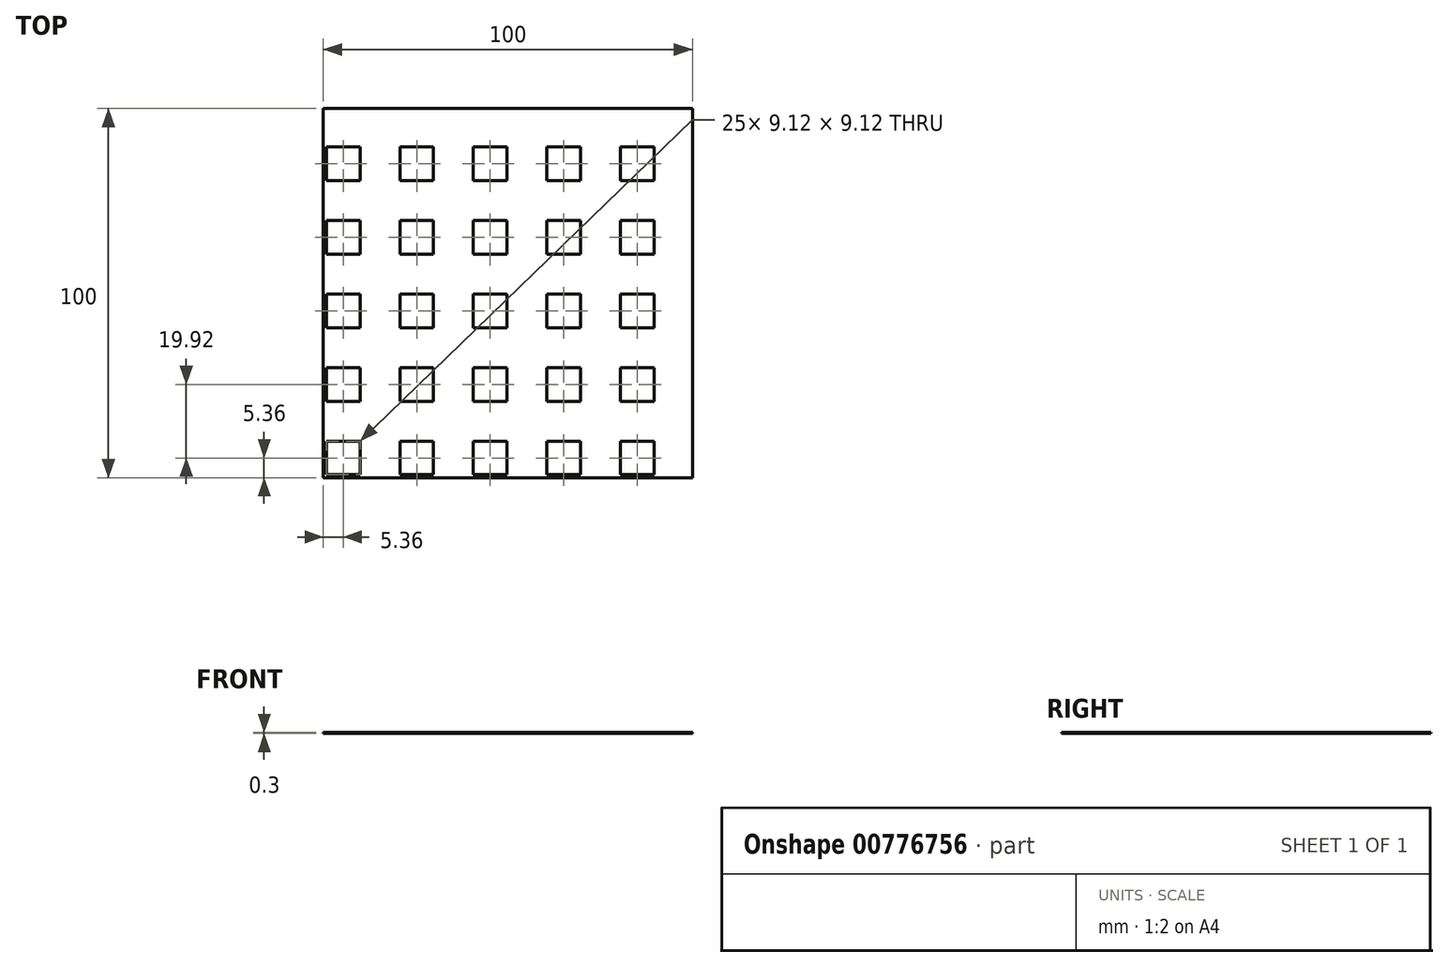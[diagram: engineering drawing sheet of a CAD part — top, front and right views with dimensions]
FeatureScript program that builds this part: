
annotation { "Feature Type Name" : "Feature", "Feature Type Description" : "" }
export const myFeature = defineFeature(function(context is Context, id is Id, definition is map)
    precondition{}
    {
        {
            var Q0;
            Q0=qCreatedBy(makeId("Top.planeOp"),FACE);
            var sketch = newSketch(context, id + "F0", { "sketchPlane" : qUnion([Q0])});
            skLineSegment(sketch, "E0.bottom", {"start": v(0, 0) * mm, "end": v(100, 0) * mm});
            skLineSegment(sketch, "E0.top", {"start": v(0, 100) * mm, "end": v(100, 100) * mm});
            skLineSegment(sketch, "E0.left", {"start": v(0, 0) * mm, "end": v(0, 100) * mm});
            skLineSegment(sketch, "E0.right", {"start": v(100, 0) * mm, "end": v(100, 100) * mm});
            skLineSegment(sketch, "E1.bottom", {"start": v(0.8, 0.8) * mm, "end": v(9.92, 0.8) * mm});
            skLineSegment(sketch, "E1.top", {"start": v(0.8, 9.92) * mm, "end": v(9.92, 9.92) * mm});
            skLineSegment(sketch, "E1.left", {"start": v(0.8, 0.8) * mm, "end": v(0.8, 9.92) * mm});
            skLineSegment(sketch, "E1.right", {"start": v(9.92, 0.8) * mm, "end": v(9.92, 9.92) * mm});
            skLineSegment(sketch, "E2.0.1.0", {"start": v(0.8, 29.84) * mm, "end": v(9.92, 29.84) * mm});
            skLineSegment(sketch, "E2.0.1.1", {"start": v(0.8, 20.72) * mm, "end": v(0.8, 29.84) * mm});
            skLineSegment(sketch, "E2.0.1.2", {"start": v(9.92, 20.72) * mm, "end": v(9.92, 29.84) * mm});
            skLineSegment(sketch, "E2.0.1.3", {"start": v(0.8, 20.72) * mm, "end": v(9.92, 20.72) * mm});
            skLineSegment(sketch, "E2.0.2.0", {"start": v(0.8, 49.76) * mm, "end": v(9.92, 49.76) * mm});
            skLineSegment(sketch, "E2.0.2.1", {"start": v(0.8, 40.64) * mm, "end": v(0.8, 49.76) * mm});
            skLineSegment(sketch, "E2.0.2.2", {"start": v(9.92, 40.64) * mm, "end": v(9.92, 49.76) * mm});
            skLineSegment(sketch, "E2.0.2.3", {"start": v(0.8, 40.64) * mm, "end": v(9.92, 40.64) * mm});
            skLineSegment(sketch, "E2.0.3.0", {"start": v(0.8, 69.68) * mm, "end": v(9.92, 69.68) * mm});
            skLineSegment(sketch, "E2.0.3.1", {"start": v(0.8, 60.56) * mm, "end": v(0.8, 69.68) * mm});
            skLineSegment(sketch, "E2.0.3.2", {"start": v(9.92, 60.56) * mm, "end": v(9.92, 69.68) * mm});
            skLineSegment(sketch, "E2.0.3.3", {"start": v(0.8, 60.56) * mm, "end": v(9.92, 60.56) * mm});
            skLineSegment(sketch, "E2.0.4.0", {"start": v(0.8, 89.6) * mm, "end": v(9.92, 89.6) * mm});
            skLineSegment(sketch, "E2.0.4.1", {"start": v(0.8, 80.48) * mm, "end": v(0.8, 89.6) * mm});
            skLineSegment(sketch, "E2.0.4.2", {"start": v(9.92, 80.48) * mm, "end": v(9.92, 89.6) * mm});
            skLineSegment(sketch, "E2.0.4.3", {"start": v(0.8, 80.48) * mm, "end": v(9.92, 80.48) * mm});
            skLineSegment(sketch, "E2.0.5.0", {"start": v(0.8, 109.52) * mm, "end": v(9.92, 109.52) * mm});
            skLineSegment(sketch, "E2.0.5.1", {"start": v(0.8, 100.4) * mm, "end": v(0.8, 109.52) * mm});
            skLineSegment(sketch, "E2.0.5.2", {"start": v(9.92, 100.4) * mm, "end": v(9.92, 109.52) * mm});
            skLineSegment(sketch, "E2.0.5.3", {"start": v(0.8, 100.4) * mm, "end": v(9.92, 100.4) * mm});
            skLineSegment(sketch, "E2.0.6.0", {"start": v(0.8, 129.44) * mm, "end": v(9.92, 129.44) * mm});
            skLineSegment(sketch, "E2.0.6.1", {"start": v(0.8, 120.32) * mm, "end": v(0.8, 129.44) * mm});
            skLineSegment(sketch, "E2.0.6.2", {"start": v(9.92, 120.32) * mm, "end": v(9.92, 129.44) * mm});
            skLineSegment(sketch, "E2.0.6.3", {"start": v(0.8, 120.32) * mm, "end": v(9.92, 120.32) * mm});
            skLineSegment(sketch, "E2.0.7.0", {"start": v(0.8, 149.36) * mm, "end": v(9.92, 149.36) * mm});
            skLineSegment(sketch, "E2.0.7.1", {"start": v(0.8, 140.24) * mm, "end": v(0.8, 149.36) * mm});
            skLineSegment(sketch, "E2.0.7.2", {"start": v(9.92, 140.24) * mm, "end": v(9.92, 149.36) * mm});
            skLineSegment(sketch, "E2.0.7.3", {"start": v(0.8, 140.24) * mm, "end": v(9.92, 140.24) * mm});
            skLineSegment(sketch, "E2.0.8.0", {"start": v(0.8, 169.28) * mm, "end": v(9.92, 169.28) * mm});
            skLineSegment(sketch, "E2.0.8.1", {"start": v(0.8, 160.16) * mm, "end": v(0.8, 169.28) * mm});
            skLineSegment(sketch, "E2.0.8.2", {"start": v(9.92, 160.16) * mm, "end": v(9.92, 169.28) * mm});
            skLineSegment(sketch, "E2.0.8.3", {"start": v(0.8, 160.16) * mm, "end": v(9.92, 160.16) * mm});
            skLineSegment(sketch, "E2.0.9.0", {"start": v(0.8, 189.2) * mm, "end": v(9.92, 189.2) * mm});
            skLineSegment(sketch, "E2.0.9.1", {"start": v(0.8, 180.08) * mm, "end": v(0.8, 189.2) * mm});
            skLineSegment(sketch, "E2.0.9.2", {"start": v(9.92, 180.08) * mm, "end": v(9.92, 189.2) * mm});
            skLineSegment(sketch, "E2.0.9.3", {"start": v(0.8, 180.08) * mm, "end": v(9.92, 180.08) * mm});
            skLineSegment(sketch, "E2.1.0.0", {"start": v(20.72, 9.92) * mm, "end": v(29.84, 9.92) * mm});
            skLineSegment(sketch, "E2.1.0.1", {"start": v(20.72, 0.8) * mm, "end": v(20.72, 9.92) * mm});
            skLineSegment(sketch, "E2.1.0.2", {"start": v(29.84, 0.8) * mm, "end": v(29.84, 9.92) * mm});
            skLineSegment(sketch, "E2.1.0.3", {"start": v(20.72, 0.8) * mm, "end": v(29.84, 0.8) * mm});
            skLineSegment(sketch, "E2.1.1.0", {"start": v(20.72, 29.84) * mm, "end": v(29.84, 29.84) * mm});
            skLineSegment(sketch, "E2.1.1.1", {"start": v(20.72, 20.72) * mm, "end": v(20.72, 29.84) * mm});
            skLineSegment(sketch, "E2.1.1.2", {"start": v(29.84, 20.72) * mm, "end": v(29.84, 29.84) * mm});
            skLineSegment(sketch, "E2.1.1.3", {"start": v(20.72, 20.72) * mm, "end": v(29.84, 20.72) * mm});
            skLineSegment(sketch, "E2.1.2.0", {"start": v(20.72, 49.76) * mm, "end": v(29.84, 49.76) * mm});
            skLineSegment(sketch, "E2.1.2.1", {"start": v(20.72, 40.64) * mm, "end": v(20.72, 49.76) * mm});
            skLineSegment(sketch, "E2.1.2.2", {"start": v(29.84, 40.64) * mm, "end": v(29.84, 49.76) * mm});
            skLineSegment(sketch, "E2.1.2.3", {"start": v(20.72, 40.64) * mm, "end": v(29.84, 40.64) * mm});
            skLineSegment(sketch, "E2.1.3.0", {"start": v(20.72, 69.68) * mm, "end": v(29.84, 69.68) * mm});
            skLineSegment(sketch, "E2.1.3.1", {"start": v(20.72, 60.56) * mm, "end": v(20.72, 69.68) * mm});
            skLineSegment(sketch, "E2.1.3.2", {"start": v(29.84, 60.56) * mm, "end": v(29.84, 69.68) * mm});
            skLineSegment(sketch, "E2.1.3.3", {"start": v(20.72, 60.56) * mm, "end": v(29.84, 60.56) * mm});
            skLineSegment(sketch, "E2.1.4.0", {"start": v(20.72, 89.6) * mm, "end": v(29.84, 89.6) * mm});
            skLineSegment(sketch, "E2.1.4.1", {"start": v(20.72, 80.48) * mm, "end": v(20.72, 89.6) * mm});
            skLineSegment(sketch, "E2.1.4.2", {"start": v(29.84, 80.48) * mm, "end": v(29.84, 89.6) * mm});
            skLineSegment(sketch, "E2.1.4.3", {"start": v(20.72, 80.48) * mm, "end": v(29.84, 80.48) * mm});
            skLineSegment(sketch, "E2.1.5.0", {"start": v(20.72, 109.52) * mm, "end": v(29.84, 109.52) * mm});
            skLineSegment(sketch, "E2.1.5.1", {"start": v(20.72, 100.4) * mm, "end": v(20.72, 109.52) * mm});
            skLineSegment(sketch, "E2.1.5.2", {"start": v(29.84, 100.4) * mm, "end": v(29.84, 109.52) * mm});
            skLineSegment(sketch, "E2.1.5.3", {"start": v(20.72, 100.4) * mm, "end": v(29.84, 100.4) * mm});
            skLineSegment(sketch, "E2.1.6.0", {"start": v(20.72, 129.44) * mm, "end": v(29.84, 129.44) * mm});
            skLineSegment(sketch, "E2.1.6.1", {"start": v(20.72, 120.32) * mm, "end": v(20.72, 129.44) * mm});
            skLineSegment(sketch, "E2.1.6.2", {"start": v(29.84, 120.32) * mm, "end": v(29.84, 129.44) * mm});
            skLineSegment(sketch, "E2.1.6.3", {"start": v(20.72, 120.32) * mm, "end": v(29.84, 120.32) * mm});
            skLineSegment(sketch, "E2.1.7.0", {"start": v(20.72, 149.36) * mm, "end": v(29.84, 149.36) * mm});
            skLineSegment(sketch, "E2.1.7.1", {"start": v(20.72, 140.24) * mm, "end": v(20.72, 149.36) * mm});
            skLineSegment(sketch, "E2.1.7.2", {"start": v(29.84, 140.24) * mm, "end": v(29.84, 149.36) * mm});
            skLineSegment(sketch, "E2.1.7.3", {"start": v(20.72, 140.24) * mm, "end": v(29.84, 140.24) * mm});
            skLineSegment(sketch, "E2.1.8.0", {"start": v(20.72, 169.28) * mm, "end": v(29.84, 169.28) * mm});
            skLineSegment(sketch, "E2.1.8.1", {"start": v(20.72, 160.16) * mm, "end": v(20.72, 169.28) * mm});
            skLineSegment(sketch, "E2.1.8.2", {"start": v(29.84, 160.16) * mm, "end": v(29.84, 169.28) * mm});
            skLineSegment(sketch, "E2.1.8.3", {"start": v(20.72, 160.16) * mm, "end": v(29.84, 160.16) * mm});
            skLineSegment(sketch, "E2.1.9.0", {"start": v(20.72, 189.2) * mm, "end": v(29.84, 189.2) * mm});
            skLineSegment(sketch, "E2.1.9.1", {"start": v(20.72, 180.08) * mm, "end": v(20.72, 189.2) * mm});
            skLineSegment(sketch, "E2.1.9.2", {"start": v(29.84, 180.08) * mm, "end": v(29.84, 189.2) * mm});
            skLineSegment(sketch, "E2.1.9.3", {"start": v(20.72, 180.08) * mm, "end": v(29.84, 180.08) * mm});
            skLineSegment(sketch, "E2.2.0.0", {"start": v(40.64, 9.92) * mm, "end": v(49.76, 9.92) * mm});
            skLineSegment(sketch, "E2.2.0.1", {"start": v(40.64, 0.8) * mm, "end": v(40.64, 9.92) * mm});
            skLineSegment(sketch, "E2.2.0.2", {"start": v(49.76, 0.8) * mm, "end": v(49.76, 9.92) * mm});
            skLineSegment(sketch, "E2.2.0.3", {"start": v(40.64, 0.8) * mm, "end": v(49.76, 0.8) * mm});
            skLineSegment(sketch, "E2.2.1.0", {"start": v(40.64, 29.84) * mm, "end": v(49.76, 29.84) * mm});
            skLineSegment(sketch, "E2.2.1.1", {"start": v(40.64, 20.72) * mm, "end": v(40.64, 29.84) * mm});
            skLineSegment(sketch, "E2.2.1.2", {"start": v(49.76, 20.72) * mm, "end": v(49.76, 29.84) * mm});
            skLineSegment(sketch, "E2.2.1.3", {"start": v(40.64, 20.72) * mm, "end": v(49.76, 20.72) * mm});
            skLineSegment(sketch, "E2.2.2.0", {"start": v(40.64, 49.76) * mm, "end": v(49.76, 49.76) * mm});
            skLineSegment(sketch, "E2.2.2.1", {"start": v(40.64, 40.64) * mm, "end": v(40.64, 49.76) * mm});
            skLineSegment(sketch, "E2.2.2.2", {"start": v(49.76, 40.64) * mm, "end": v(49.76, 49.76) * mm});
            skLineSegment(sketch, "E2.2.2.3", {"start": v(40.64, 40.64) * mm, "end": v(49.76, 40.64) * mm});
            skLineSegment(sketch, "E2.2.3.0", {"start": v(40.64, 69.68) * mm, "end": v(49.76, 69.68) * mm});
            skLineSegment(sketch, "E2.2.3.1", {"start": v(40.64, 60.56) * mm, "end": v(40.64, 69.68) * mm});
            skLineSegment(sketch, "E2.2.3.2", {"start": v(49.76, 60.56) * mm, "end": v(49.76, 69.68) * mm});
            skLineSegment(sketch, "E2.2.3.3", {"start": v(40.64, 60.56) * mm, "end": v(49.76, 60.56) * mm});
            skLineSegment(sketch, "E2.2.4.0", {"start": v(40.64, 89.6) * mm, "end": v(49.76, 89.6) * mm});
            skLineSegment(sketch, "E2.2.4.1", {"start": v(40.64, 80.48) * mm, "end": v(40.64, 89.6) * mm});
            skLineSegment(sketch, "E2.2.4.2", {"start": v(49.76, 80.48) * mm, "end": v(49.76, 89.6) * mm});
            skLineSegment(sketch, "E2.2.4.3", {"start": v(40.64, 80.48) * mm, "end": v(49.76, 80.48) * mm});
            skLineSegment(sketch, "E2.2.5.0", {"start": v(40.64, 109.52) * mm, "end": v(49.76, 109.52) * mm});
            skLineSegment(sketch, "E2.2.5.1", {"start": v(40.64, 100.4) * mm, "end": v(40.64, 109.52) * mm});
            skLineSegment(sketch, "E2.2.5.2", {"start": v(49.76, 100.4) * mm, "end": v(49.76, 109.52) * mm});
            skLineSegment(sketch, "E2.2.5.3", {"start": v(40.64, 100.4) * mm, "end": v(49.76, 100.4) * mm});
            skLineSegment(sketch, "E2.2.6.0", {"start": v(40.64, 129.44) * mm, "end": v(49.76, 129.44) * mm});
            skLineSegment(sketch, "E2.2.6.1", {"start": v(40.64, 120.32) * mm, "end": v(40.64, 129.44) * mm});
            skLineSegment(sketch, "E2.2.6.2", {"start": v(49.76, 120.32) * mm, "end": v(49.76, 129.44) * mm});
            skLineSegment(sketch, "E2.2.6.3", {"start": v(40.64, 120.32) * mm, "end": v(49.76, 120.32) * mm});
            skLineSegment(sketch, "E2.2.7.0", {"start": v(40.64, 149.36) * mm, "end": v(49.76, 149.36) * mm});
            skLineSegment(sketch, "E2.2.7.1", {"start": v(40.64, 140.24) * mm, "end": v(40.64, 149.36) * mm});
            skLineSegment(sketch, "E2.2.7.2", {"start": v(49.76, 140.24) * mm, "end": v(49.76, 149.36) * mm});
            skLineSegment(sketch, "E2.2.7.3", {"start": v(40.64, 140.24) * mm, "end": v(49.76, 140.24) * mm});
            skLineSegment(sketch, "E2.2.8.0", {"start": v(40.64, 169.28) * mm, "end": v(49.76, 169.28) * mm});
            skLineSegment(sketch, "E2.2.8.1", {"start": v(40.64, 160.16) * mm, "end": v(40.64, 169.28) * mm});
            skLineSegment(sketch, "E2.2.8.2", {"start": v(49.76, 160.16) * mm, "end": v(49.76, 169.28) * mm});
            skLineSegment(sketch, "E2.2.8.3", {"start": v(40.64, 160.16) * mm, "end": v(49.76, 160.16) * mm});
            skLineSegment(sketch, "E2.2.9.0", {"start": v(40.64, 189.2) * mm, "end": v(49.76, 189.2) * mm});
            skLineSegment(sketch, "E2.2.9.1", {"start": v(40.64, 180.08) * mm, "end": v(40.64, 189.2) * mm});
            skLineSegment(sketch, "E2.2.9.2", {"start": v(49.76, 180.08) * mm, "end": v(49.76, 189.2) * mm});
            skLineSegment(sketch, "E2.2.9.3", {"start": v(40.64, 180.08) * mm, "end": v(49.76, 180.08) * mm});
            skLineSegment(sketch, "E2.3.0.0", {"start": v(60.56, 9.92) * mm, "end": v(69.68, 9.92) * mm});
            skLineSegment(sketch, "E2.3.0.1", {"start": v(60.56, 0.8) * mm, "end": v(60.56, 9.92) * mm});
            skLineSegment(sketch, "E2.3.0.2", {"start": v(69.68, 0.8) * mm, "end": v(69.68, 9.92) * mm});
            skLineSegment(sketch, "E2.3.0.3", {"start": v(60.56, 0.8) * mm, "end": v(69.68, 0.8) * mm});
            skLineSegment(sketch, "E2.3.1.0", {"start": v(60.56, 29.84) * mm, "end": v(69.68, 29.84) * mm});
            skLineSegment(sketch, "E2.3.1.1", {"start": v(60.56, 20.72) * mm, "end": v(60.56, 29.84) * mm});
            skLineSegment(sketch, "E2.3.1.2", {"start": v(69.68, 20.72) * mm, "end": v(69.68, 29.84) * mm});
            skLineSegment(sketch, "E2.3.1.3", {"start": v(60.56, 20.72) * mm, "end": v(69.68, 20.72) * mm});
            skLineSegment(sketch, "E2.3.2.0", {"start": v(60.56, 49.76) * mm, "end": v(69.68, 49.76) * mm});
            skLineSegment(sketch, "E2.3.2.1", {"start": v(60.56, 40.64) * mm, "end": v(60.56, 49.76) * mm});
            skLineSegment(sketch, "E2.3.2.2", {"start": v(69.68, 40.64) * mm, "end": v(69.68, 49.76) * mm});
            skLineSegment(sketch, "E2.3.2.3", {"start": v(60.56, 40.64) * mm, "end": v(69.68, 40.64) * mm});
            skLineSegment(sketch, "E2.3.3.0", {"start": v(60.56, 69.68) * mm, "end": v(69.68, 69.68) * mm});
            skLineSegment(sketch, "E2.3.3.1", {"start": v(60.56, 60.56) * mm, "end": v(60.56, 69.68) * mm});
            skLineSegment(sketch, "E2.3.3.2", {"start": v(69.68, 60.56) * mm, "end": v(69.68, 69.68) * mm});
            skLineSegment(sketch, "E2.3.3.3", {"start": v(60.56, 60.56) * mm, "end": v(69.68, 60.56) * mm});
            skLineSegment(sketch, "E2.3.4.0", {"start": v(60.56, 89.6) * mm, "end": v(69.68, 89.6) * mm});
            skLineSegment(sketch, "E2.3.4.1", {"start": v(60.56, 80.48) * mm, "end": v(60.56, 89.6) * mm});
            skLineSegment(sketch, "E2.3.4.2", {"start": v(69.68, 80.48) * mm, "end": v(69.68, 89.6) * mm});
            skLineSegment(sketch, "E2.3.4.3", {"start": v(60.56, 80.48) * mm, "end": v(69.68, 80.48) * mm});
            skLineSegment(sketch, "E2.3.5.0", {"start": v(60.56, 109.52) * mm, "end": v(69.68, 109.52) * mm});
            skLineSegment(sketch, "E2.3.5.1", {"start": v(60.56, 100.4) * mm, "end": v(60.56, 109.52) * mm});
            skLineSegment(sketch, "E2.3.5.2", {"start": v(69.68, 100.4) * mm, "end": v(69.68, 109.52) * mm});
            skLineSegment(sketch, "E2.3.5.3", {"start": v(60.56, 100.4) * mm, "end": v(69.68, 100.4) * mm});
            skLineSegment(sketch, "E2.3.6.0", {"start": v(60.56, 129.44) * mm, "end": v(69.68, 129.44) * mm});
            skLineSegment(sketch, "E2.3.6.1", {"start": v(60.56, 120.32) * mm, "end": v(60.56, 129.44) * mm});
            skLineSegment(sketch, "E2.3.6.2", {"start": v(69.68, 120.32) * mm, "end": v(69.68, 129.44) * mm});
            skLineSegment(sketch, "E2.3.6.3", {"start": v(60.56, 120.32) * mm, "end": v(69.68, 120.32) * mm});
            skLineSegment(sketch, "E2.3.7.0", {"start": v(60.56, 149.36) * mm, "end": v(69.68, 149.36) * mm});
            skLineSegment(sketch, "E2.3.7.1", {"start": v(60.56, 140.24) * mm, "end": v(60.56, 149.36) * mm});
            skLineSegment(sketch, "E2.3.7.2", {"start": v(69.68, 140.24) * mm, "end": v(69.68, 149.36) * mm});
            skLineSegment(sketch, "E2.3.7.3", {"start": v(60.56, 140.24) * mm, "end": v(69.68, 140.24) * mm});
            skLineSegment(sketch, "E2.3.8.0", {"start": v(60.56, 169.28) * mm, "end": v(69.68, 169.28) * mm});
            skLineSegment(sketch, "E2.3.8.1", {"start": v(60.56, 160.16) * mm, "end": v(60.56, 169.28) * mm});
            skLineSegment(sketch, "E2.3.8.2", {"start": v(69.68, 160.16) * mm, "end": v(69.68, 169.28) * mm});
            skLineSegment(sketch, "E2.3.8.3", {"start": v(60.56, 160.16) * mm, "end": v(69.68, 160.16) * mm});
            skLineSegment(sketch, "E2.3.9.0", {"start": v(60.56, 189.2) * mm, "end": v(69.68, 189.2) * mm});
            skLineSegment(sketch, "E2.3.9.1", {"start": v(60.56, 180.08) * mm, "end": v(60.56, 189.2) * mm});
            skLineSegment(sketch, "E2.3.9.2", {"start": v(69.68, 180.08) * mm, "end": v(69.68, 189.2) * mm});
            skLineSegment(sketch, "E2.3.9.3", {"start": v(60.56, 180.08) * mm, "end": v(69.68, 180.08) * mm});
            skLineSegment(sketch, "E2.4.0.0", {"start": v(80.48, 9.92) * mm, "end": v(89.6, 9.92) * mm});
            skLineSegment(sketch, "E2.4.0.1", {"start": v(80.48, 0.8) * mm, "end": v(80.48, 9.92) * mm});
            skLineSegment(sketch, "E2.4.0.2", {"start": v(89.6, 0.8) * mm, "end": v(89.6, 9.92) * mm});
            skLineSegment(sketch, "E2.4.0.3", {"start": v(80.48, 0.8) * mm, "end": v(89.6, 0.8) * mm});
            skLineSegment(sketch, "E2.4.1.0", {"start": v(80.48, 29.84) * mm, "end": v(89.6, 29.84) * mm});
            skLineSegment(sketch, "E2.4.1.1", {"start": v(80.48, 20.72) * mm, "end": v(80.48, 29.84) * mm});
            skLineSegment(sketch, "E2.4.1.2", {"start": v(89.6, 20.72) * mm, "end": v(89.6, 29.84) * mm});
            skLineSegment(sketch, "E2.4.1.3", {"start": v(80.48, 20.72) * mm, "end": v(89.6, 20.72) * mm});
            skLineSegment(sketch, "E2.4.2.0", {"start": v(80.48, 49.76) * mm, "end": v(89.6, 49.76) * mm});
            skLineSegment(sketch, "E2.4.2.1", {"start": v(80.48, 40.64) * mm, "end": v(80.48, 49.76) * mm});
            skLineSegment(sketch, "E2.4.2.2", {"start": v(89.6, 40.64) * mm, "end": v(89.6, 49.76) * mm});
            skLineSegment(sketch, "E2.4.2.3", {"start": v(80.48, 40.64) * mm, "end": v(89.6, 40.64) * mm});
            skLineSegment(sketch, "E2.4.3.0", {"start": v(80.48, 69.68) * mm, "end": v(89.6, 69.68) * mm});
            skLineSegment(sketch, "E2.4.3.1", {"start": v(80.48, 60.56) * mm, "end": v(80.48, 69.68) * mm});
            skLineSegment(sketch, "E2.4.3.2", {"start": v(89.6, 60.56) * mm, "end": v(89.6, 69.68) * mm});
            skLineSegment(sketch, "E2.4.3.3", {"start": v(80.48, 60.56) * mm, "end": v(89.6, 60.56) * mm});
            skLineSegment(sketch, "E2.4.4.0", {"start": v(80.48, 89.6) * mm, "end": v(89.6, 89.6) * mm});
            skLineSegment(sketch, "E2.4.4.1", {"start": v(80.48, 80.48) * mm, "end": v(80.48, 89.6) * mm});
            skLineSegment(sketch, "E2.4.4.2", {"start": v(89.6, 80.48) * mm, "end": v(89.6, 89.6) * mm});
            skLineSegment(sketch, "E2.4.4.3", {"start": v(80.48, 80.48) * mm, "end": v(89.6, 80.48) * mm});
            skLineSegment(sketch, "E2.4.5.0", {"start": v(80.48, 109.52) * mm, "end": v(89.6, 109.52) * mm});
            skLineSegment(sketch, "E2.4.5.1", {"start": v(80.48, 100.4) * mm, "end": v(80.48, 109.52) * mm});
            skLineSegment(sketch, "E2.4.5.2", {"start": v(89.6, 100.4) * mm, "end": v(89.6, 109.52) * mm});
            skLineSegment(sketch, "E2.4.5.3", {"start": v(80.48, 100.4) * mm, "end": v(89.6, 100.4) * mm});
            skLineSegment(sketch, "E2.4.6.0", {"start": v(80.48, 129.44) * mm, "end": v(89.6, 129.44) * mm});
            skLineSegment(sketch, "E2.4.6.1", {"start": v(80.48, 120.32) * mm, "end": v(80.48, 129.44) * mm});
            skLineSegment(sketch, "E2.4.6.2", {"start": v(89.6, 120.32) * mm, "end": v(89.6, 129.44) * mm});
            skLineSegment(sketch, "E2.4.6.3", {"start": v(80.48, 120.32) * mm, "end": v(89.6, 120.32) * mm});
            skLineSegment(sketch, "E2.4.7.0", {"start": v(80.48, 149.36) * mm, "end": v(89.6, 149.36) * mm});
            skLineSegment(sketch, "E2.4.7.1", {"start": v(80.48, 140.24) * mm, "end": v(80.48, 149.36) * mm});
            skLineSegment(sketch, "E2.4.7.2", {"start": v(89.6, 140.24) * mm, "end": v(89.6, 149.36) * mm});
            skLineSegment(sketch, "E2.4.7.3", {"start": v(80.48, 140.24) * mm, "end": v(89.6, 140.24) * mm});
            skLineSegment(sketch, "E2.4.8.0", {"start": v(80.48, 169.28) * mm, "end": v(89.6, 169.28) * mm});
            skLineSegment(sketch, "E2.4.8.1", {"start": v(80.48, 160.16) * mm, "end": v(80.48, 169.28) * mm});
            skLineSegment(sketch, "E2.4.8.2", {"start": v(89.6, 160.16) * mm, "end": v(89.6, 169.28) * mm});
            skLineSegment(sketch, "E2.4.8.3", {"start": v(80.48, 160.16) * mm, "end": v(89.6, 160.16) * mm});
            skLineSegment(sketch, "E2.4.9.0", {"start": v(80.48, 189.2) * mm, "end": v(89.6, 189.2) * mm});
            skLineSegment(sketch, "E2.4.9.1", {"start": v(80.48, 180.08) * mm, "end": v(80.48, 189.2) * mm});
            skLineSegment(sketch, "E2.4.9.2", {"start": v(89.6, 180.08) * mm, "end": v(89.6, 189.2) * mm});
            skLineSegment(sketch, "E2.4.9.3", {"start": v(80.48, 180.08) * mm, "end": v(89.6, 180.08) * mm});
            skLineSegment(sketch, "E2.5.0.0", {"start": v(100.4, 9.92) * mm, "end": v(109.52, 9.92) * mm});
            skLineSegment(sketch, "E2.5.0.1", {"start": v(100.4, 0.8) * mm, "end": v(100.4, 9.92) * mm});
            skLineSegment(sketch, "E2.5.0.2", {"start": v(109.52, 0.8) * mm, "end": v(109.52, 9.92) * mm});
            skLineSegment(sketch, "E2.5.0.3", {"start": v(100.4, 0.8) * mm, "end": v(109.52, 0.8) * mm});
            skLineSegment(sketch, "E2.5.1.0", {"start": v(100.4, 29.84) * mm, "end": v(109.52, 29.84) * mm});
            skLineSegment(sketch, "E2.5.1.1", {"start": v(100.4, 20.72) * mm, "end": v(100.4, 29.84) * mm});
            skLineSegment(sketch, "E2.5.1.2", {"start": v(109.52, 20.72) * mm, "end": v(109.52, 29.84) * mm});
            skLineSegment(sketch, "E2.5.1.3", {"start": v(100.4, 20.72) * mm, "end": v(109.52, 20.72) * mm});
            skLineSegment(sketch, "E2.5.2.0", {"start": v(100.4, 49.76) * mm, "end": v(109.52, 49.76) * mm});
            skLineSegment(sketch, "E2.5.2.1", {"start": v(100.4, 40.64) * mm, "end": v(100.4, 49.76) * mm});
            skLineSegment(sketch, "E2.5.2.2", {"start": v(109.52, 40.64) * mm, "end": v(109.52, 49.76) * mm});
            skLineSegment(sketch, "E2.5.2.3", {"start": v(100.4, 40.64) * mm, "end": v(109.52, 40.64) * mm});
            skLineSegment(sketch, "E2.5.3.0", {"start": v(100.4, 69.68) * mm, "end": v(109.52, 69.68) * mm});
            skLineSegment(sketch, "E2.5.3.1", {"start": v(100.4, 60.56) * mm, "end": v(100.4, 69.68) * mm});
            skLineSegment(sketch, "E2.5.3.2", {"start": v(109.52, 60.56) * mm, "end": v(109.52, 69.68) * mm});
            skLineSegment(sketch, "E2.5.3.3", {"start": v(100.4, 60.56) * mm, "end": v(109.52, 60.56) * mm});
            skLineSegment(sketch, "E2.5.4.0", {"start": v(100.4, 89.6) * mm, "end": v(109.52, 89.6) * mm});
            skLineSegment(sketch, "E2.5.4.1", {"start": v(100.4, 80.48) * mm, "end": v(100.4, 89.6) * mm});
            skLineSegment(sketch, "E2.5.4.2", {"start": v(109.52, 80.48) * mm, "end": v(109.52, 89.6) * mm});
            skLineSegment(sketch, "E2.5.4.3", {"start": v(100.4, 80.48) * mm, "end": v(109.52, 80.48) * mm});
            skLineSegment(sketch, "E2.5.5.0", {"start": v(100.4, 109.52) * mm, "end": v(109.52, 109.52) * mm});
            skLineSegment(sketch, "E2.5.5.1", {"start": v(100.4, 100.4) * mm, "end": v(100.4, 109.52) * mm});
            skLineSegment(sketch, "E2.5.5.2", {"start": v(109.52, 100.4) * mm, "end": v(109.52, 109.52) * mm});
            skLineSegment(sketch, "E2.5.5.3", {"start": v(100.4, 100.4) * mm, "end": v(109.52, 100.4) * mm});
            skLineSegment(sketch, "E2.5.6.0", {"start": v(100.4, 129.44) * mm, "end": v(109.52, 129.44) * mm});
            skLineSegment(sketch, "E2.5.6.1", {"start": v(100.4, 120.32) * mm, "end": v(100.4, 129.44) * mm});
            skLineSegment(sketch, "E2.5.6.2", {"start": v(109.52, 120.32) * mm, "end": v(109.52, 129.44) * mm});
            skLineSegment(sketch, "E2.5.6.3", {"start": v(100.4, 120.32) * mm, "end": v(109.52, 120.32) * mm});
            skLineSegment(sketch, "E2.5.7.0", {"start": v(100.4, 149.36) * mm, "end": v(109.52, 149.36) * mm});
            skLineSegment(sketch, "E2.5.7.1", {"start": v(100.4, 140.24) * mm, "end": v(100.4, 149.36) * mm});
            skLineSegment(sketch, "E2.5.7.2", {"start": v(109.52, 140.24) * mm, "end": v(109.52, 149.36) * mm});
            skLineSegment(sketch, "E2.5.7.3", {"start": v(100.4, 140.24) * mm, "end": v(109.52, 140.24) * mm});
            skLineSegment(sketch, "E2.5.8.0", {"start": v(100.4, 169.28) * mm, "end": v(109.52, 169.28) * mm});
            skLineSegment(sketch, "E2.5.8.1", {"start": v(100.4, 160.16) * mm, "end": v(100.4, 169.28) * mm});
            skLineSegment(sketch, "E2.5.8.2", {"start": v(109.52, 160.16) * mm, "end": v(109.52, 169.28) * mm});
            skLineSegment(sketch, "E2.5.8.3", {"start": v(100.4, 160.16) * mm, "end": v(109.52, 160.16) * mm});
            skLineSegment(sketch, "E2.5.9.0", {"start": v(100.4, 189.2) * mm, "end": v(109.52, 189.2) * mm});
            skLineSegment(sketch, "E2.5.9.1", {"start": v(100.4, 180.08) * mm, "end": v(100.4, 189.2) * mm});
            skLineSegment(sketch, "E2.5.9.2", {"start": v(109.52, 180.08) * mm, "end": v(109.52, 189.2) * mm});
            skLineSegment(sketch, "E2.5.9.3", {"start": v(100.4, 180.08) * mm, "end": v(109.52, 180.08) * mm});
            skLineSegment(sketch, "E2.6.0.0", {"start": v(120.32, 9.92) * mm, "end": v(129.44, 9.92) * mm});
            skLineSegment(sketch, "E2.6.0.1", {"start": v(120.32, 0.8) * mm, "end": v(120.32, 9.92) * mm});
            skLineSegment(sketch, "E2.6.0.2", {"start": v(129.44, 0.8) * mm, "end": v(129.44, 9.92) * mm});
            skLineSegment(sketch, "E2.6.0.3", {"start": v(120.32, 0.8) * mm, "end": v(129.44, 0.8) * mm});
            skLineSegment(sketch, "E2.6.1.0", {"start": v(120.32, 29.84) * mm, "end": v(129.44, 29.84) * mm});
            skLineSegment(sketch, "E2.6.1.1", {"start": v(120.32, 20.72) * mm, "end": v(120.32, 29.84) * mm});
            skLineSegment(sketch, "E2.6.1.2", {"start": v(129.44, 20.72) * mm, "end": v(129.44, 29.84) * mm});
            skLineSegment(sketch, "E2.6.1.3", {"start": v(120.32, 20.72) * mm, "end": v(129.44, 20.72) * mm});
            skLineSegment(sketch, "E2.6.2.0", {"start": v(120.32, 49.76) * mm, "end": v(129.44, 49.76) * mm});
            skLineSegment(sketch, "E2.6.2.1", {"start": v(120.32, 40.64) * mm, "end": v(120.32, 49.76) * mm});
            skLineSegment(sketch, "E2.6.2.2", {"start": v(129.44, 40.64) * mm, "end": v(129.44, 49.76) * mm});
            skLineSegment(sketch, "E2.6.2.3", {"start": v(120.32, 40.64) * mm, "end": v(129.44, 40.64) * mm});
            skLineSegment(sketch, "E2.6.3.0", {"start": v(120.32, 69.68) * mm, "end": v(129.44, 69.68) * mm});
            skLineSegment(sketch, "E2.6.3.1", {"start": v(120.32, 60.56) * mm, "end": v(120.32, 69.68) * mm});
            skLineSegment(sketch, "E2.6.3.2", {"start": v(129.44, 60.56) * mm, "end": v(129.44, 69.68) * mm});
            skLineSegment(sketch, "E2.6.3.3", {"start": v(120.32, 60.56) * mm, "end": v(129.44, 60.56) * mm});
            skLineSegment(sketch, "E2.6.4.0", {"start": v(120.32, 89.6) * mm, "end": v(129.44, 89.6) * mm});
            skLineSegment(sketch, "E2.6.4.1", {"start": v(120.32, 80.48) * mm, "end": v(120.32, 89.6) * mm});
            skLineSegment(sketch, "E2.6.4.2", {"start": v(129.44, 80.48) * mm, "end": v(129.44, 89.6) * mm});
            skLineSegment(sketch, "E2.6.4.3", {"start": v(120.32, 80.48) * mm, "end": v(129.44, 80.48) * mm});
            skLineSegment(sketch, "E2.6.5.0", {"start": v(120.32, 109.52) * mm, "end": v(129.44, 109.52) * mm});
            skLineSegment(sketch, "E2.6.5.1", {"start": v(120.32, 100.4) * mm, "end": v(120.32, 109.52) * mm});
            skLineSegment(sketch, "E2.6.5.2", {"start": v(129.44, 100.4) * mm, "end": v(129.44, 109.52) * mm});
            skLineSegment(sketch, "E2.6.5.3", {"start": v(120.32, 100.4) * mm, "end": v(129.44, 100.4) * mm});
            skLineSegment(sketch, "E2.6.6.0", {"start": v(120.32, 129.44) * mm, "end": v(129.44, 129.44) * mm});
            skLineSegment(sketch, "E2.6.6.1", {"start": v(120.32, 120.32) * mm, "end": v(120.32, 129.44) * mm});
            skLineSegment(sketch, "E2.6.6.2", {"start": v(129.44, 120.32) * mm, "end": v(129.44, 129.44) * mm});
            skLineSegment(sketch, "E2.6.6.3", {"start": v(120.32, 120.32) * mm, "end": v(129.44, 120.32) * mm});
            skLineSegment(sketch, "E2.6.7.0", {"start": v(120.32, 149.36) * mm, "end": v(129.44, 149.36) * mm});
            skLineSegment(sketch, "E2.6.7.1", {"start": v(120.32, 140.24) * mm, "end": v(120.32, 149.36) * mm});
            skLineSegment(sketch, "E2.6.7.2", {"start": v(129.44, 140.24) * mm, "end": v(129.44, 149.36) * mm});
            skLineSegment(sketch, "E2.6.7.3", {"start": v(120.32, 140.24) * mm, "end": v(129.44, 140.24) * mm});
            skLineSegment(sketch, "E2.6.8.0", {"start": v(120.32, 169.28) * mm, "end": v(129.44, 169.28) * mm});
            skLineSegment(sketch, "E2.6.8.1", {"start": v(120.32, 160.16) * mm, "end": v(120.32, 169.28) * mm});
            skLineSegment(sketch, "E2.6.8.2", {"start": v(129.44, 160.16) * mm, "end": v(129.44, 169.28) * mm});
            skLineSegment(sketch, "E2.6.8.3", {"start": v(120.32, 160.16) * mm, "end": v(129.44, 160.16) * mm});
            skLineSegment(sketch, "E2.6.9.0", {"start": v(120.32, 189.2) * mm, "end": v(129.44, 189.2) * mm});
            skLineSegment(sketch, "E2.6.9.1", {"start": v(120.32, 180.08) * mm, "end": v(120.32, 189.2) * mm});
            skLineSegment(sketch, "E2.6.9.2", {"start": v(129.44, 180.08) * mm, "end": v(129.44, 189.2) * mm});
            skLineSegment(sketch, "E2.6.9.3", {"start": v(120.32, 180.08) * mm, "end": v(129.44, 180.08) * mm});
            skLineSegment(sketch, "E2.7.0.0", {"start": v(140.24, 9.92) * mm, "end": v(149.36, 9.92) * mm});
            skLineSegment(sketch, "E2.7.0.1", {"start": v(140.24, 0.8) * mm, "end": v(140.24, 9.92) * mm});
            skLineSegment(sketch, "E2.7.0.2", {"start": v(149.36, 0.8) * mm, "end": v(149.36, 9.92) * mm});
            skLineSegment(sketch, "E2.7.0.3", {"start": v(140.24, 0.8) * mm, "end": v(149.36, 0.8) * mm});
            skLineSegment(sketch, "E2.7.1.0", {"start": v(140.24, 29.84) * mm, "end": v(149.36, 29.84) * mm});
            skLineSegment(sketch, "E2.7.1.1", {"start": v(140.24, 20.72) * mm, "end": v(140.24, 29.84) * mm});
            skLineSegment(sketch, "E2.7.1.2", {"start": v(149.36, 20.72) * mm, "end": v(149.36, 29.84) * mm});
            skLineSegment(sketch, "E2.7.1.3", {"start": v(140.24, 20.72) * mm, "end": v(149.36, 20.72) * mm});
            skLineSegment(sketch, "E2.7.2.0", {"start": v(140.24, 49.76) * mm, "end": v(149.36, 49.76) * mm});
            skLineSegment(sketch, "E2.7.2.1", {"start": v(140.24, 40.64) * mm, "end": v(140.24, 49.76) * mm});
            skLineSegment(sketch, "E2.7.2.2", {"start": v(149.36, 40.64) * mm, "end": v(149.36, 49.76) * mm});
            skLineSegment(sketch, "E2.7.2.3", {"start": v(140.24, 40.64) * mm, "end": v(149.36, 40.64) * mm});
            skLineSegment(sketch, "E2.7.3.0", {"start": v(140.24, 69.68) * mm, "end": v(149.36, 69.68) * mm});
            skLineSegment(sketch, "E2.7.3.1", {"start": v(140.24, 60.56) * mm, "end": v(140.24, 69.68) * mm});
            skLineSegment(sketch, "E2.7.3.2", {"start": v(149.36, 60.56) * mm, "end": v(149.36, 69.68) * mm});
            skLineSegment(sketch, "E2.7.3.3", {"start": v(140.24, 60.56) * mm, "end": v(149.36, 60.56) * mm});
            skLineSegment(sketch, "E2.7.4.0", {"start": v(140.24, 89.6) * mm, "end": v(149.36, 89.6) * mm});
            skLineSegment(sketch, "E2.7.4.1", {"start": v(140.24, 80.48) * mm, "end": v(140.24, 89.6) * mm});
            skLineSegment(sketch, "E2.7.4.2", {"start": v(149.36, 80.48) * mm, "end": v(149.36, 89.6) * mm});
            skLineSegment(sketch, "E2.7.4.3", {"start": v(140.24, 80.48) * mm, "end": v(149.36, 80.48) * mm});
            skLineSegment(sketch, "E2.7.5.0", {"start": v(140.24, 109.52) * mm, "end": v(149.36, 109.52) * mm});
            skLineSegment(sketch, "E2.7.5.1", {"start": v(140.24, 100.4) * mm, "end": v(140.24, 109.52) * mm});
            skLineSegment(sketch, "E2.7.5.2", {"start": v(149.36, 100.4) * mm, "end": v(149.36, 109.52) * mm});
            skLineSegment(sketch, "E2.7.5.3", {"start": v(140.24, 100.4) * mm, "end": v(149.36, 100.4) * mm});
            skLineSegment(sketch, "E2.7.6.0", {"start": v(140.24, 129.44) * mm, "end": v(149.36, 129.44) * mm});
            skLineSegment(sketch, "E2.7.6.1", {"start": v(140.24, 120.32) * mm, "end": v(140.24, 129.44) * mm});
            skLineSegment(sketch, "E2.7.6.2", {"start": v(149.36, 120.32) * mm, "end": v(149.36, 129.44) * mm});
            skLineSegment(sketch, "E2.7.6.3", {"start": v(140.24, 120.32) * mm, "end": v(149.36, 120.32) * mm});
            skLineSegment(sketch, "E2.7.7.0", {"start": v(140.24, 149.36) * mm, "end": v(149.36, 149.36) * mm});
            skLineSegment(sketch, "E2.7.7.1", {"start": v(140.24, 140.24) * mm, "end": v(140.24, 149.36) * mm});
            skLineSegment(sketch, "E2.7.7.2", {"start": v(149.36, 140.24) * mm, "end": v(149.36, 149.36) * mm});
            skLineSegment(sketch, "E2.7.7.3", {"start": v(140.24, 140.24) * mm, "end": v(149.36, 140.24) * mm});
            skLineSegment(sketch, "E2.7.8.0", {"start": v(140.24, 169.28) * mm, "end": v(149.36, 169.28) * mm});
            skLineSegment(sketch, "E2.7.8.1", {"start": v(140.24, 160.16) * mm, "end": v(140.24, 169.28) * mm});
            skLineSegment(sketch, "E2.7.8.2", {"start": v(149.36, 160.16) * mm, "end": v(149.36, 169.28) * mm});
            skLineSegment(sketch, "E2.7.8.3", {"start": v(140.24, 160.16) * mm, "end": v(149.36, 160.16) * mm});
            skLineSegment(sketch, "E2.7.9.0", {"start": v(140.24, 189.2) * mm, "end": v(149.36, 189.2) * mm});
            skLineSegment(sketch, "E2.7.9.1", {"start": v(140.24, 180.08) * mm, "end": v(140.24, 189.2) * mm});
            skLineSegment(sketch, "E2.7.9.2", {"start": v(149.36, 180.08) * mm, "end": v(149.36, 189.2) * mm});
            skLineSegment(sketch, "E2.7.9.3", {"start": v(140.24, 180.08) * mm, "end": v(149.36, 180.08) * mm});
            skLineSegment(sketch, "E2.8.0.0", {"start": v(160.16, 9.92) * mm, "end": v(169.28, 9.92) * mm});
            skLineSegment(sketch, "E2.8.0.1", {"start": v(160.16, 0.8) * mm, "end": v(160.16, 9.92) * mm});
            skLineSegment(sketch, "E2.8.0.2", {"start": v(169.28, 0.8) * mm, "end": v(169.28, 9.92) * mm});
            skLineSegment(sketch, "E2.8.0.3", {"start": v(160.16, 0.8) * mm, "end": v(169.28, 0.8) * mm});
            skLineSegment(sketch, "E2.8.1.0", {"start": v(160.16, 29.84) * mm, "end": v(169.28, 29.84) * mm});
            skLineSegment(sketch, "E2.8.1.1", {"start": v(160.16, 20.72) * mm, "end": v(160.16, 29.84) * mm});
            skLineSegment(sketch, "E2.8.1.2", {"start": v(169.28, 20.72) * mm, "end": v(169.28, 29.84) * mm});
            skLineSegment(sketch, "E2.8.1.3", {"start": v(160.16, 20.72) * mm, "end": v(169.28, 20.72) * mm});
            skLineSegment(sketch, "E2.8.2.0", {"start": v(160.16, 49.76) * mm, "end": v(169.28, 49.76) * mm});
            skLineSegment(sketch, "E2.8.2.1", {"start": v(160.16, 40.64) * mm, "end": v(160.16, 49.76) * mm});
            skLineSegment(sketch, "E2.8.2.2", {"start": v(169.28, 40.64) * mm, "end": v(169.28, 49.76) * mm});
            skLineSegment(sketch, "E2.8.2.3", {"start": v(160.16, 40.64) * mm, "end": v(169.28, 40.64) * mm});
            skLineSegment(sketch, "E2.8.3.0", {"start": v(160.16, 69.68) * mm, "end": v(169.28, 69.68) * mm});
            skLineSegment(sketch, "E2.8.3.1", {"start": v(160.16, 60.56) * mm, "end": v(160.16, 69.68) * mm});
            skLineSegment(sketch, "E2.8.3.2", {"start": v(169.28, 60.56) * mm, "end": v(169.28, 69.68) * mm});
            skLineSegment(sketch, "E2.8.3.3", {"start": v(160.16, 60.56) * mm, "end": v(169.28, 60.56) * mm});
            skLineSegment(sketch, "E2.8.4.0", {"start": v(160.16, 89.6) * mm, "end": v(169.28, 89.6) * mm});
            skLineSegment(sketch, "E2.8.4.1", {"start": v(160.16, 80.48) * mm, "end": v(160.16, 89.6) * mm});
            skLineSegment(sketch, "E2.8.4.2", {"start": v(169.28, 80.48) * mm, "end": v(169.28, 89.6) * mm});
            skLineSegment(sketch, "E2.8.4.3", {"start": v(160.16, 80.48) * mm, "end": v(169.28, 80.48) * mm});
            skLineSegment(sketch, "E2.8.5.0", {"start": v(160.16, 109.52) * mm, "end": v(169.28, 109.52) * mm});
            skLineSegment(sketch, "E2.8.5.1", {"start": v(160.16, 100.4) * mm, "end": v(160.16, 109.52) * mm});
            skLineSegment(sketch, "E2.8.5.2", {"start": v(169.28, 100.4) * mm, "end": v(169.28, 109.52) * mm});
            skLineSegment(sketch, "E2.8.5.3", {"start": v(160.16, 100.4) * mm, "end": v(169.28, 100.4) * mm});
            skLineSegment(sketch, "E2.8.6.0", {"start": v(160.16, 129.44) * mm, "end": v(169.28, 129.44) * mm});
            skLineSegment(sketch, "E2.8.6.1", {"start": v(160.16, 120.32) * mm, "end": v(160.16, 129.44) * mm});
            skLineSegment(sketch, "E2.8.6.2", {"start": v(169.28, 120.32) * mm, "end": v(169.28, 129.44) * mm});
            skLineSegment(sketch, "E2.8.6.3", {"start": v(160.16, 120.32) * mm, "end": v(169.28, 120.32) * mm});
            skLineSegment(sketch, "E2.8.7.0", {"start": v(160.16, 149.36) * mm, "end": v(169.28, 149.36) * mm});
            skLineSegment(sketch, "E2.8.7.1", {"start": v(160.16, 140.24) * mm, "end": v(160.16, 149.36) * mm});
            skLineSegment(sketch, "E2.8.7.2", {"start": v(169.28, 140.24) * mm, "end": v(169.28, 149.36) * mm});
            skLineSegment(sketch, "E2.8.7.3", {"start": v(160.16, 140.24) * mm, "end": v(169.28, 140.24) * mm});
            skLineSegment(sketch, "E2.8.8.0", {"start": v(160.16, 169.28) * mm, "end": v(169.28, 169.28) * mm});
            skLineSegment(sketch, "E2.8.8.1", {"start": v(160.16, 160.16) * mm, "end": v(160.16, 169.28) * mm});
            skLineSegment(sketch, "E2.8.8.2", {"start": v(169.28, 160.16) * mm, "end": v(169.28, 169.28) * mm});
            skLineSegment(sketch, "E2.8.8.3", {"start": v(160.16, 160.16) * mm, "end": v(169.28, 160.16) * mm});
            skLineSegment(sketch, "E2.8.9.0", {"start": v(160.16, 189.2) * mm, "end": v(169.28, 189.2) * mm});
            skLineSegment(sketch, "E2.8.9.1", {"start": v(160.16, 180.08) * mm, "end": v(160.16, 189.2) * mm});
            skLineSegment(sketch, "E2.8.9.2", {"start": v(169.28, 180.08) * mm, "end": v(169.28, 189.2) * mm});
            skLineSegment(sketch, "E2.8.9.3", {"start": v(160.16, 180.08) * mm, "end": v(169.28, 180.08) * mm});
            skLineSegment(sketch, "E2.9.0.0", {"start": v(180.08, 9.92) * mm, "end": v(189.2, 9.92) * mm});
            skLineSegment(sketch, "E2.9.0.1", {"start": v(180.08, 0.8) * mm, "end": v(180.08, 9.92) * mm});
            skLineSegment(sketch, "E2.9.0.2", {"start": v(189.2, 0.8) * mm, "end": v(189.2, 9.92) * mm});
            skLineSegment(sketch, "E2.9.0.3", {"start": v(180.08, 0.8) * mm, "end": v(189.2, 0.8) * mm});
            skLineSegment(sketch, "E2.9.1.0", {"start": v(180.08, 29.84) * mm, "end": v(189.2, 29.84) * mm});
            skLineSegment(sketch, "E2.9.1.1", {"start": v(180.08, 20.72) * mm, "end": v(180.08, 29.84) * mm});
            skLineSegment(sketch, "E2.9.1.2", {"start": v(189.2, 20.72) * mm, "end": v(189.2, 29.84) * mm});
            skLineSegment(sketch, "E2.9.1.3", {"start": v(180.08, 20.72) * mm, "end": v(189.2, 20.72) * mm});
            skLineSegment(sketch, "E2.9.2.0", {"start": v(180.08, 49.76) * mm, "end": v(189.2, 49.76) * mm});
            skLineSegment(sketch, "E2.9.2.1", {"start": v(180.08, 40.64) * mm, "end": v(180.08, 49.76) * mm});
            skLineSegment(sketch, "E2.9.2.2", {"start": v(189.2, 40.64) * mm, "end": v(189.2, 49.76) * mm});
            skLineSegment(sketch, "E2.9.2.3", {"start": v(180.08, 40.64) * mm, "end": v(189.2, 40.64) * mm});
            skLineSegment(sketch, "E2.9.3.0", {"start": v(180.08, 69.68) * mm, "end": v(189.2, 69.68) * mm});
            skLineSegment(sketch, "E2.9.3.1", {"start": v(180.08, 60.56) * mm, "end": v(180.08, 69.68) * mm});
            skLineSegment(sketch, "E2.9.3.2", {"start": v(189.2, 60.56) * mm, "end": v(189.2, 69.68) * mm});
            skLineSegment(sketch, "E2.9.3.3", {"start": v(180.08, 60.56) * mm, "end": v(189.2, 60.56) * mm});
            skLineSegment(sketch, "E2.9.4.0", {"start": v(180.08, 89.6) * mm, "end": v(189.2, 89.6) * mm});
            skLineSegment(sketch, "E2.9.4.1", {"start": v(180.08, 80.48) * mm, "end": v(180.08, 89.6) * mm});
            skLineSegment(sketch, "E2.9.4.2", {"start": v(189.2, 80.48) * mm, "end": v(189.2, 89.6) * mm});
            skLineSegment(sketch, "E2.9.4.3", {"start": v(180.08, 80.48) * mm, "end": v(189.2, 80.48) * mm});
            skLineSegment(sketch, "E2.9.5.0", {"start": v(180.08, 109.52) * mm, "end": v(189.2, 109.52) * mm});
            skLineSegment(sketch, "E2.9.5.1", {"start": v(180.08, 100.4) * mm, "end": v(180.08, 109.52) * mm});
            skLineSegment(sketch, "E2.9.5.2", {"start": v(189.2, 100.4) * mm, "end": v(189.2, 109.52) * mm});
            skLineSegment(sketch, "E2.9.5.3", {"start": v(180.08, 100.4) * mm, "end": v(189.2, 100.4) * mm});
            skLineSegment(sketch, "E2.9.6.0", {"start": v(180.08, 129.44) * mm, "end": v(189.2, 129.44) * mm});
            skLineSegment(sketch, "E2.9.6.1", {"start": v(180.08, 120.32) * mm, "end": v(180.08, 129.44) * mm});
            skLineSegment(sketch, "E2.9.6.2", {"start": v(189.2, 120.32) * mm, "end": v(189.2, 129.44) * mm});
            skLineSegment(sketch, "E2.9.6.3", {"start": v(180.08, 120.32) * mm, "end": v(189.2, 120.32) * mm});
            skLineSegment(sketch, "E2.9.7.0", {"start": v(180.08, 149.36) * mm, "end": v(189.2, 149.36) * mm});
            skLineSegment(sketch, "E2.9.7.1", {"start": v(180.08, 140.24) * mm, "end": v(180.08, 149.36) * mm});
            skLineSegment(sketch, "E2.9.7.2", {"start": v(189.2, 140.24) * mm, "end": v(189.2, 149.36) * mm});
            skLineSegment(sketch, "E2.9.7.3", {"start": v(180.08, 140.24) * mm, "end": v(189.2, 140.24) * mm});
            skLineSegment(sketch, "E2.9.8.0", {"start": v(180.08, 169.28) * mm, "end": v(189.2, 169.28) * mm});
            skLineSegment(sketch, "E2.9.8.1", {"start": v(180.08, 160.16) * mm, "end": v(180.08, 169.28) * mm});
            skLineSegment(sketch, "E2.9.8.2", {"start": v(189.2, 160.16) * mm, "end": v(189.2, 169.28) * mm});
            skLineSegment(sketch, "E2.9.8.3", {"start": v(180.08, 160.16) * mm, "end": v(189.2, 160.16) * mm});
            skLineSegment(sketch, "E2.9.9.0", {"start": v(180.08, 189.2) * mm, "end": v(189.2, 189.2) * mm});
            skLineSegment(sketch, "E2.9.9.1", {"start": v(180.08, 180.08) * mm, "end": v(180.08, 189.2) * mm});
            skLineSegment(sketch, "E2.9.9.2", {"start": v(189.2, 180.08) * mm, "end": v(189.2, 189.2) * mm});
            skLineSegment(sketch, "E2.9.9.3", {"start": v(180.08, 180.08) * mm, "end": v(189.2, 180.08) * mm});
            skLineSegment(sketch, "E2.direction1", {"start": v(0.8, 20.8) * mm, "end": v(20.72, 20.8) * mm, "construction": true});
            skLineSegment(sketch, "E2.direction2", {"start": v(0.8, 20.8) * mm, "end": v(0.8, 40.72) * mm, "construction": true});
            skSolve(sketch);
        }
        {
            var Q0;
            Q0=makeQuery(id+"F0.imprint","IMPRINT",FACE,{"disambiguationData":[TD([[makeQuery(id+"F0.imprint","IMPRINT",EDGE,{"derivedFrom":sQuery(id+"F0.wireOp",EDGE,"E0.bottom")}),1.0]])]});
            extrude(context, id + "F1", {"entities" : qUnion([Q0]), "depth" : 0.3 * mm, "offsetDistance" : 25 * mm});
        }
    });
